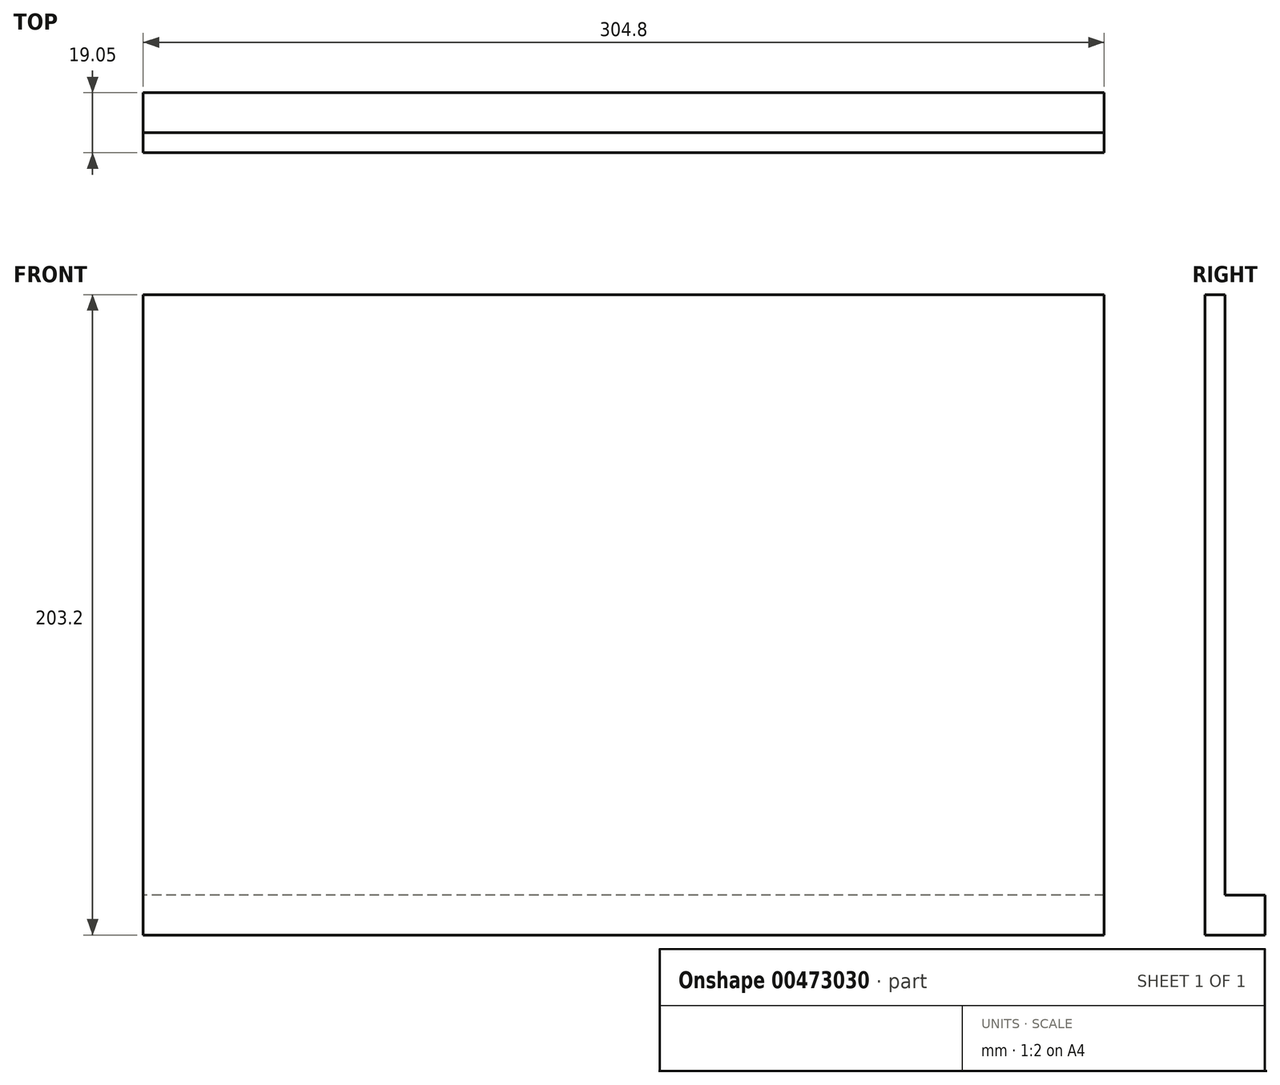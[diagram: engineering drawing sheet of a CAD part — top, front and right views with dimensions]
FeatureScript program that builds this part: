
annotation { "Feature Type Name" : "Feature", "Feature Type Description" : "" }
export const myFeature = defineFeature(function(context is Context, id is Id, definition is map)
    precondition{}
    {
        {
            var Q0;
            Q0=qCreatedBy(makeId("Front.planeOp"),FACE);
            var sketch = newSketch(context, id + "F0", { "sketchPlane" : qUnion([Q0])});
            skLineSegment(sketch, "E0.bottom", {"start": v(152.4, 101.6) * mm, "end": v(-152.4, 101.6) * mm});
            skLineSegment(sketch, "E0.top", {"start": v(152.4, -101.6) * mm, "end": v(-152.4, -101.6) * mm});
            skLineSegment(sketch, "E0.left", {"start": v(152.4, 101.6) * mm, "end": v(152.4, -101.6) * mm});
            skLineSegment(sketch, "E0.right", {"start": v(-152.4, 101.6) * mm, "end": v(-152.4, -101.6) * mm});
            skPoint(sketch, "E0.middle", {"position": v(0, 0) * mm});
            skSolve(sketch);
        }
        {
            var Q0;
            Q0=makeQuery(id+"F0.imprint","IMPRINT",FACE,{"disambiguationData":[TD([[makeQuery(id+"F0.imprint","IMPRINT",EDGE,{"derivedFrom":sQuery(id+"F0.wireOp",EDGE,"E0.bottom")}),1.0]])]});
            extrude(context, id + "F1", {"entities" : qUnion([Q0]), "depth" : 6.35 * mm});
        }
        {
            var Q0;
            Q0=makeQuery(id+"F1.opExtrude","CAP_FACE",FACE,{"disambiguationData":[OSD([sQuery(id+"F0.wireOp",EDGE,"E0.bottom"),sQuery(id+"F0.wireOp",EDGE,"E0.top"),sQuery(id+"F0.wireOp",EDGE,"E0.left"),sQuery(id+"F0.wireOp",EDGE,"E0.right")])],"isStart":true});
            var sketch = newSketch(context, id + "F2", { "sketchPlane" : qUnion([Q0])});
            skLineSegment(sketch, "E1.bottom", {"start": v(-152.4, -101.6) * mm, "end": v(152.4, -101.6) * mm});
            skLineSegment(sketch, "E1.top", {"start": v(-152.4, -88.9) * mm, "end": v(152.4, -88.9) * mm});
            skLineSegment(sketch, "E1.left", {"start": v(-152.4, -101.6) * mm, "end": v(-152.4, -88.9) * mm});
            skLineSegment(sketch, "E1.right", {"start": v(152.4, -101.6) * mm, "end": v(152.4, -88.9) * mm});
            skSolve(sketch);
        }
        {
            var Q0;
            Q0 = qSketchRegion(id + "F2", true);
            var Q1;
            Q1=makeQuery(id+"F2.imprint","IMPRINT",FACE,{"disambiguationData":[TD([[makeQuery(id+"F2.imprint","IMPRINT",EDGE,{"derivedFrom":sQuery(id+"F2.wireOp",EDGE,"E1.bottom")}),1.0]])]});
            extrude(context, id + "F3", {"entities" : qUnion([Q0, Q1]), "operationType" : NewBodyOperationType.ADD, "depth" : 12.7 * mm});
        }
    });
